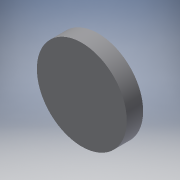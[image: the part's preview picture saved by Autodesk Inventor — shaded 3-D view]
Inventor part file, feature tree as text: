
AUTODESK INVENTOR PART (.ipt)
format: ipt  version: 2016 (Build 200138000, 138)  size: 97,280 bytes
history: native  units: in
note: dims shown in document units (in); Inventor stores cm internally (conversion verified against a paired STEP export)
features: extrude x2, sketch x2, reference x1
ambient origin geometry x8: Origin, YZ Plane, XZ Plane, XY Plane, X Axis, Y Axis, Z Axis, Center Point
bodies: Solid1 (feature_tree)
feature tree (5):
  extrude  "Extrusion1"  Depth=0.0394in TaperAngle=0.0deg
  extrude  "Extrusion2"  Depth=0.2362in TaperAngle=0.0deg
  sketch  "Sketch1"  dims[d0=0.2165in d1=0.0394in d2=0.0in]
  reference  "Reference1"
  sketch  "Sketch2"  dims[d3=0.1575in d4=0.2362in d5=0.0in]
